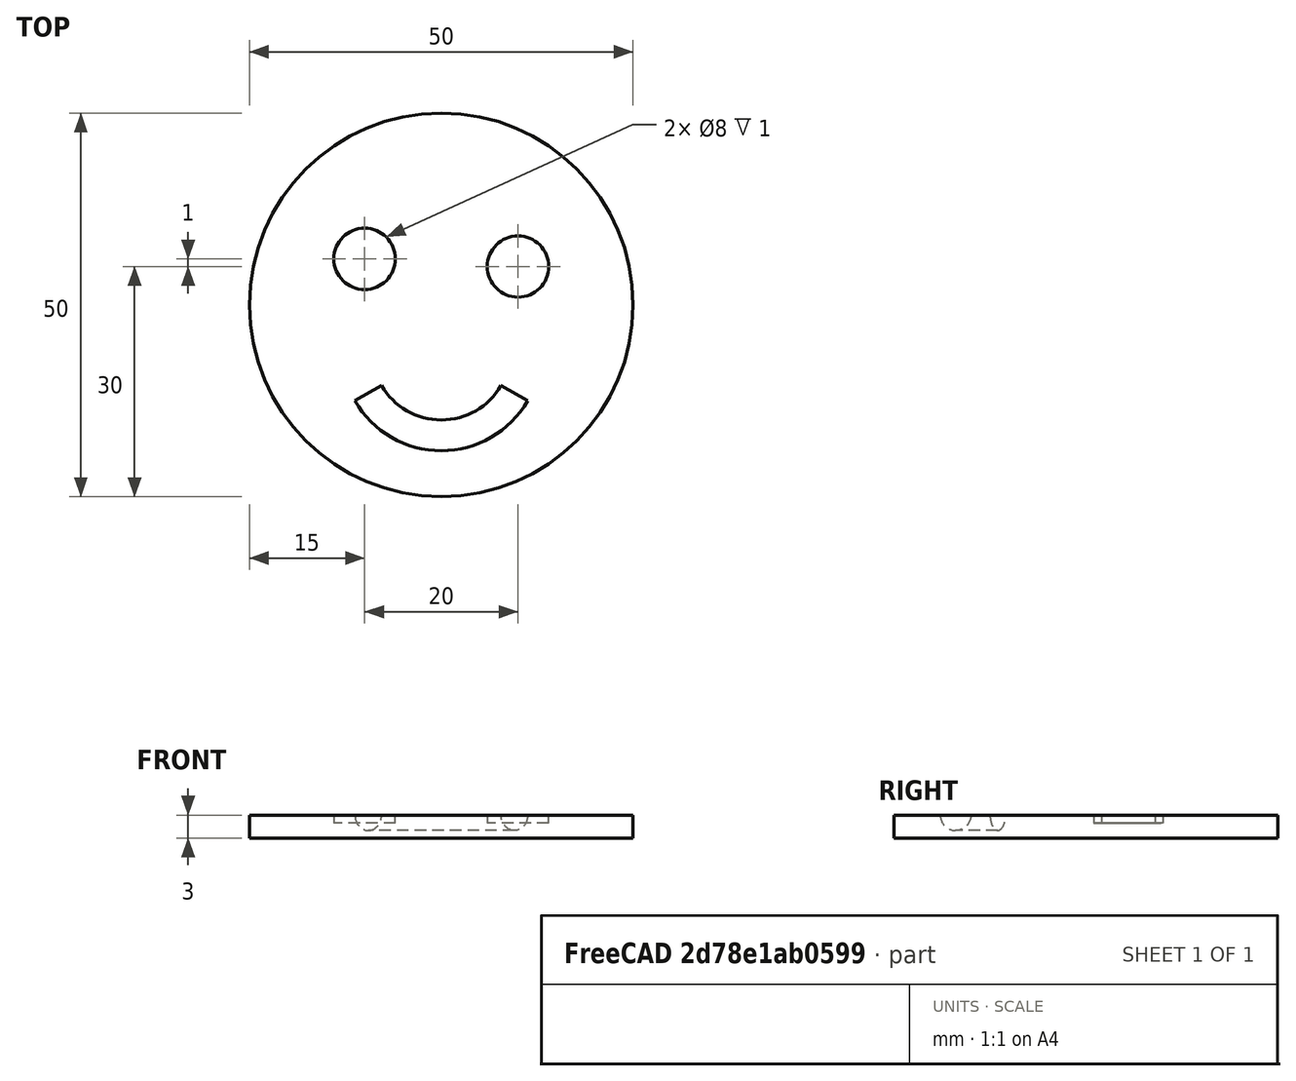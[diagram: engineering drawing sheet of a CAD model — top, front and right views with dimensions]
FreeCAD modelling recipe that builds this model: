
FCSTD DOCUMENT  (FreeCAD 1.0R39319 (Git))
Label: ojt1_t15r01_smile
License: All rights reserved
LicenseURL: https://en.wikipedia.org/wiki/All_rights_reserved
objects: Part::Cylinder×3, Part::Cut×3, Part::Torus×1
note: 7 computed .brp shape members not serialized (recipe doc carries the construction recipe); baked Part::Feature solids carry a one-line shape summary decoded from their .brp

FEATURE [Part::Cylinder] Cylinder  label="Cilindre"
  Angle = 360
  AttacherType = Attacher::AttachEngine3D
  FirstAngle = 0
  Height = 3
  Radius = 25
  SecondAngle = 0
FEATURE [Part::Cylinder] Cylinder001  label="Cilindre001"
  Angle = 360
  AttacherType = Attacher::AttachEngine3D
  FirstAngle = 0
  Height = 4
  Placement = pos=(-10,6,2) rot=(0,0,1;0rad)
  Radius = 4
  SecondAngle = 0
FEATURE [Part::Cut] Cut
  Base = -> Cylinder
  Refine = true
  Tool = -> Cylinder001
FEATURE [Part::Cylinder] Cylinder002  label="Cilindre002"
  Angle = 360
  AttacherType = Attacher::AttachEngine3D
  FirstAngle = 0
  Height = 4
  Placement = pos=(10,5,2) rot=(0,0,1;0rad)
  Radius = 4
  SecondAngle = 0
FEATURE [Part::Cut] Cut001
  Base = -> Cut
  Placement = pos=(0,0,2) rot=(0,0,1;0rad)
  Refine = true
  Tool = -> Cylinder002
FEATURE [Part::Torus] Torus
  Angle1 = -180
  Angle2 = 180
  Angle3 = 120
  AttacherType = Attacher::AttachEngine3D
  Placement = pos=(0,-6,5) rot=(0,0,-1;2.61799rad)
  Radius1 = 11
  Radius2 = 2
FEATURE [Part::Cut] Cut002
  Base = -> Cut001
  Refine = true
  Tool = -> Torus
